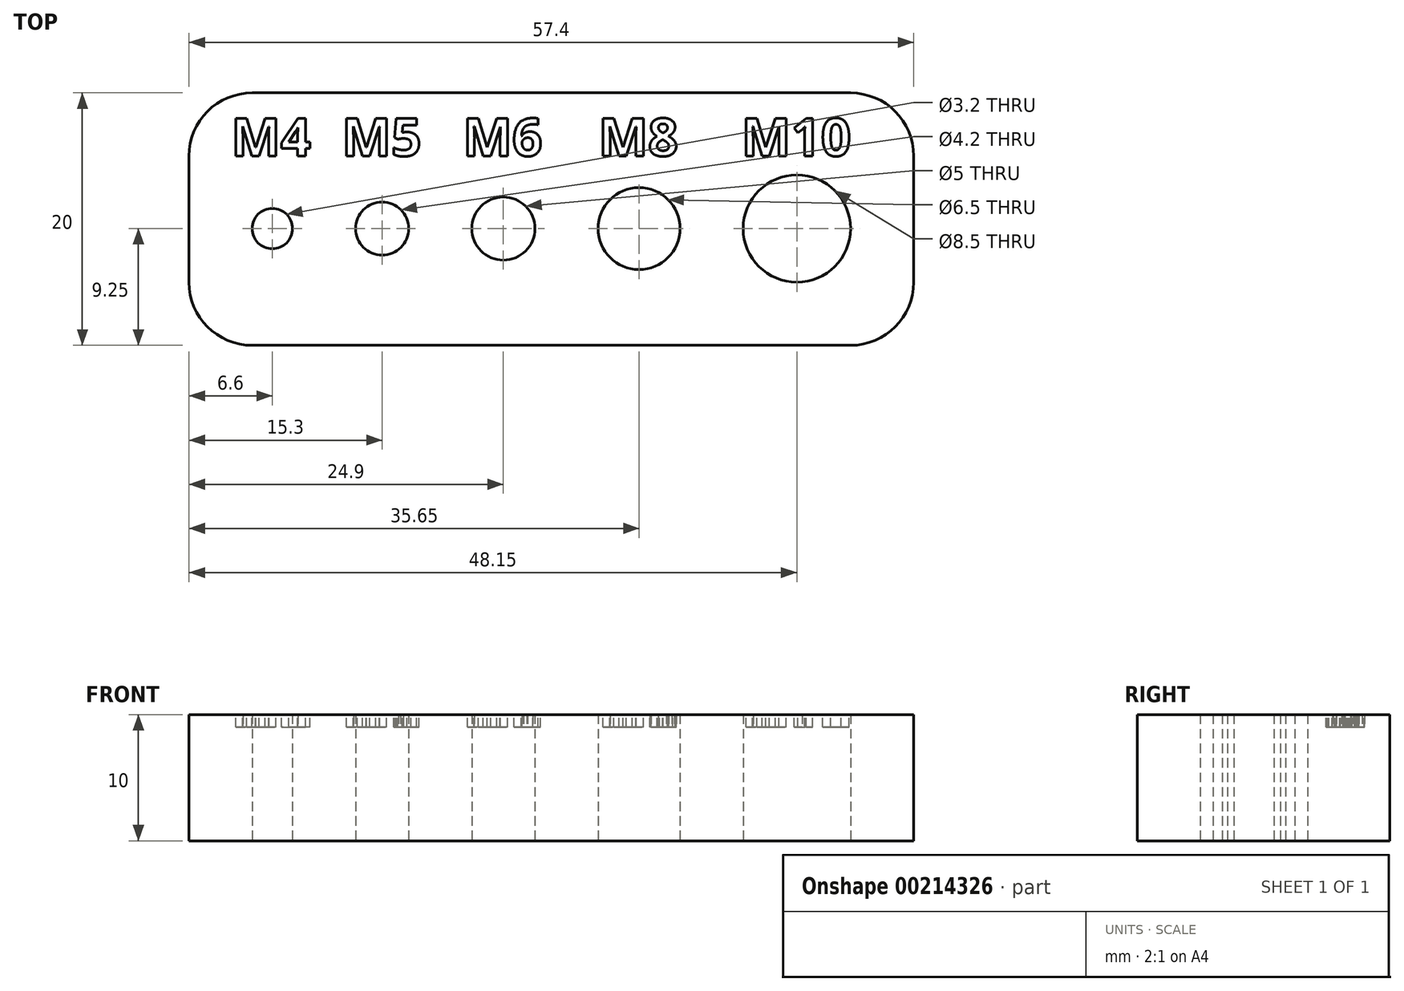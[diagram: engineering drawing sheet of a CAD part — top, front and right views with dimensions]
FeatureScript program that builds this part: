
annotation { "Feature Type Name" : "Feature", "Feature Type Description" : "" }
export const myFeature = defineFeature(function(context is Context, id is Id, definition is map)
    precondition{}
    {
        {
            var Q0;
            Q0=qCreatedBy(makeId("Top.planeOp"),FACE);
            var sketch = newSketch(context, id + "F0", { "sketchPlane" : qUnion([Q0])});
            skLineSegment(sketch, "E0.bottom", {"start": v(-24.9, 10.75) * mm, "end": v(32.5, 10.75) * mm});
            skLineSegment(sketch, "E0.top", {"start": v(-24.9, -9.25) * mm, "end": v(32.5, -9.25) * mm});
            skLineSegment(sketch, "E0.left", {"start": v(-24.9, 10.75) * mm, "end": v(-24.9, -9.25) * mm});
            skLineSegment(sketch, "E0.right", {"start": v(32.5, 10.75) * mm, "end": v(32.5, -9.25) * mm});
            skCircle(sketch, "E1", {"center": v(-18.3, 0) * mm, "radius": 1.6 * mm});
            skCircle(sketch, "E2", {"center": v(-9.6, 0) * mm, "radius": 2.1 * mm});
            skCircle(sketch, "E3", {"center": v(0, 0) * mm, "radius": 2.5 * mm});
            skCircle(sketch, "E4", {"center": v(10.75, 0) * mm, "radius": 3.25 * mm});
            skCircle(sketch, "E5", {"center": v(23.25, 0) * mm, "radius": 4.25 * mm});
            skSolve(sketch);
        }
        {
            var Q0;
            Q0=makeQuery(id+"F0.imprint","IMPRINT",FACE,{"disambiguationData":[TD([[makeQuery(id+"F0.imprint","IMPRINT",EDGE,{"derivedFrom":sQuery(id+"F0.wireOp",EDGE,"E0.bottom")}),-1.0]])]});
            extrude(context, id + "F1", {"entities" : qUnion([Q0]), "depth" : 10 * mm, "offsetDistance" : 25 * mm});
        }
        {
            var Q0;
            Q0=makeQuery(id+"F1.opExtrude","CAP_FACE",FACE,{"disambiguationData":[OSD([sQuery(id+"F0.wireOp",EDGE,"E0.bottom"),sQuery(id+"F0.wireOp",EDGE,"E0.top"),sQuery(id+"F0.wireOp",EDGE,"E0.left"),sQuery(id+"F0.wireOp",EDGE,"E0.right"),sQuery(id+"F0.wireOp",EDGE,"E1"),sQuery(id+"F0.wireOp",EDGE,"E2"),sQuery(id+"F0.wireOp",EDGE,"E3"),sQuery(id+"F0.wireOp",EDGE,"E4"),sQuery(id+"F0.wireOp",EDGE,"E5")])],"isStart":false});
            var sketch = newSketch(context, id + "F2", { "sketchPlane" : qUnion([Q0])});
            skText(sketch, "E6", { "text": "M4", "fontName": "OpenSans-Bold.ttf"});
            skPoint(sketch, "E7", {"position": v(-18.3, 0) * mm});
            skPoint(sketch, "E8", {"position": v(-9.6, 0) * mm});
            skPoint(sketch, "E9", {"position": v(10.75, 0) * mm});
            skPoint(sketch, "E10", {"position": v(23.25, 0) * mm});
            skText(sketch, "E11", { "text": "M5", "fontName": "OpenSans-Bold.ttf"});
            skText(sketch, "E12", { "text": "M6", "fontName": "OpenSans-Bold.ttf"});
            skText(sketch, "E13", { "text": "M8", "fontName": "OpenSans-Bold.ttf"});
            skText(sketch, "E14", { "text": "M10", "fontName": "OpenSans-Bold.ttf"});
            const initialGuessF2  = {"E6": [-0.02156, 0.00575, 1, 0, 0.003], "E11": [-0.0128, 0.00575, 1, 0, 0.003], "E12": [-0.00322, 0.00575, 1, 0, 0.003], "E13": [0.00753, 0.00575, 1, 0, 0.003], "E14": [0.01885, 0.00575, 1, 0, 0.003]};
            skSetInitialGuess(sketch, initialGuessF2);
            skSolve(sketch);
        }
        {
            var Q0;
            Q0 = qSketchRegion(id + "F2", true);
            extrude(context, id + "F3", {"entities" : qUnion([Q0]), "operationType" : NewBodyOperationType.REMOVE, "oppositeDirection" : true, "depth" : 1 * mm});
        }
        {
            var Q0;
            Q0=makeQuery(id+"F1.opExtrude","SWEPT_EDGE",EDGE,{"disambiguationData":[OSD([sQuery(id+"F0.wireOp",EDGE,"E0.top"),sQuery(id+"F0.wireOp",EDGE,"E0.right")])]});
            var Q1;
            Q1=makeQuery(id+"F1.opExtrude","SWEPT_EDGE",EDGE,{"disambiguationData":[OSD([sQuery(id+"F0.wireOp",EDGE,"E0.bottom"),sQuery(id+"F0.wireOp",EDGE,"E0.right")])]});
            var Q2;
            Q2=makeQuery(id+"F1.opExtrude","SWEPT_EDGE",EDGE,{"disambiguationData":[OSD([sQuery(id+"F0.wireOp",EDGE,"E0.bottom"),sQuery(id+"F0.wireOp",EDGE,"E0.left")])]});
            var Q3;
            Q3=makeQuery(id+"F1.opExtrude","SWEPT_EDGE",EDGE,{"disambiguationData":[OSD([sQuery(id+"F0.wireOp",EDGE,"E0.top"),sQuery(id+"F0.wireOp",EDGE,"E0.left")])]});
            fillet(context, id + "F4", {"entities" : qUnion([Q0, Q1, Q2, Q3]), "radius" : 5 * mm, "tangentPropagation" : true, "allowEdgeOverflow" : false});
        }
    });
